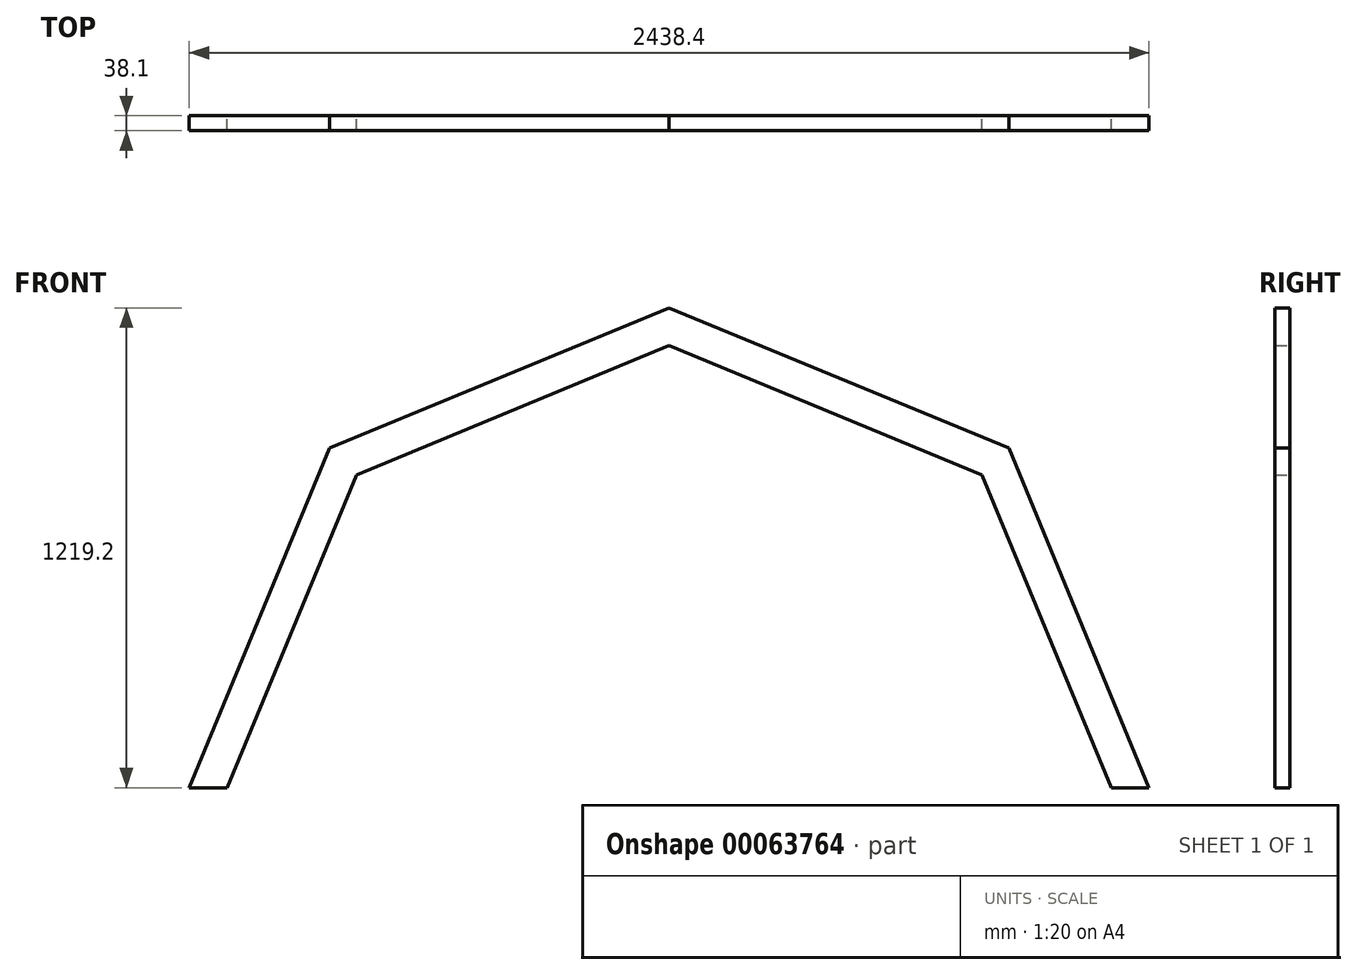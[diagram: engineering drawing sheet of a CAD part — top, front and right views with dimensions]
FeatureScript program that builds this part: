
annotation { "Feature Type Name" : "Feature", "Feature Type Description" : "" }
export const myFeature = defineFeature(function(context is Context, id is Id, definition is map)
    precondition{}
    {
        {
            var Q0;
            Q0=qCreatedBy(makeId("Front.planeOp"),FACE);
            var sketch = newSketch(context, id + "F0", { "sketchPlane" : qUnion([Q0])});
            skLineSegment(sketch, "E0.top", {"start": v(-1027.18, -196.14) * mm, "end": v(-930.98, -196.14) * mm});
            skLineSegment(sketch, "E1", {"start": v(-1027.18, -196.14) * mm, "end": v(-670.66, 666.55) * mm});
            skLineSegment(sketch, "E2", {"start": v(-670.66, 666.55) * mm, "end": v(192.02, 1023.06) * mm});
            skLineSegment(sketch, "E3", {"start": v(-930.98, -196.14) * mm, "end": v(-602.6, 598.48) * mm});
            skLineSegment(sketch, "E4", {"start": v(-602.6, 598.48) * mm, "end": v(192.02, 926.87) * mm});
            skLineSegment(sketch, "E5.top", {"start": v(1315.03, -196.14) * mm, "end": v(1411.22, -196.14) * mm});
            skLineSegment(sketch, "E6.MirrorCS", {"start": v(1315.03, -196.14) * mm, "end": v(986.64, 598.48) * mm});
            skLineSegment(sketch, "E7.MirrorCS", {"start": v(1411.22, -196.14) * mm, "end": v(1054.7, 666.55) * mm});
            skLineSegment(sketch, "E8.MirrorCS", {"start": v(986.64, 598.48) * mm, "end": v(192.02, 926.87) * mm});
            skLineSegment(sketch, "E9.MirrorCS", {"start": v(1054.7, 666.55) * mm, "end": v(192.02, 1023.06) * mm});
            skSolve(sketch);
        }
        {
            var Q0;
            Q0 = qSketchRegion(id + "F0", true);
            extrude(context, id + "F1", {"entities" : qUnion([Q0]), "endBound" : BoundingType.SYMMETRIC, "depth" : 38.1 * mm});
        }
    });
